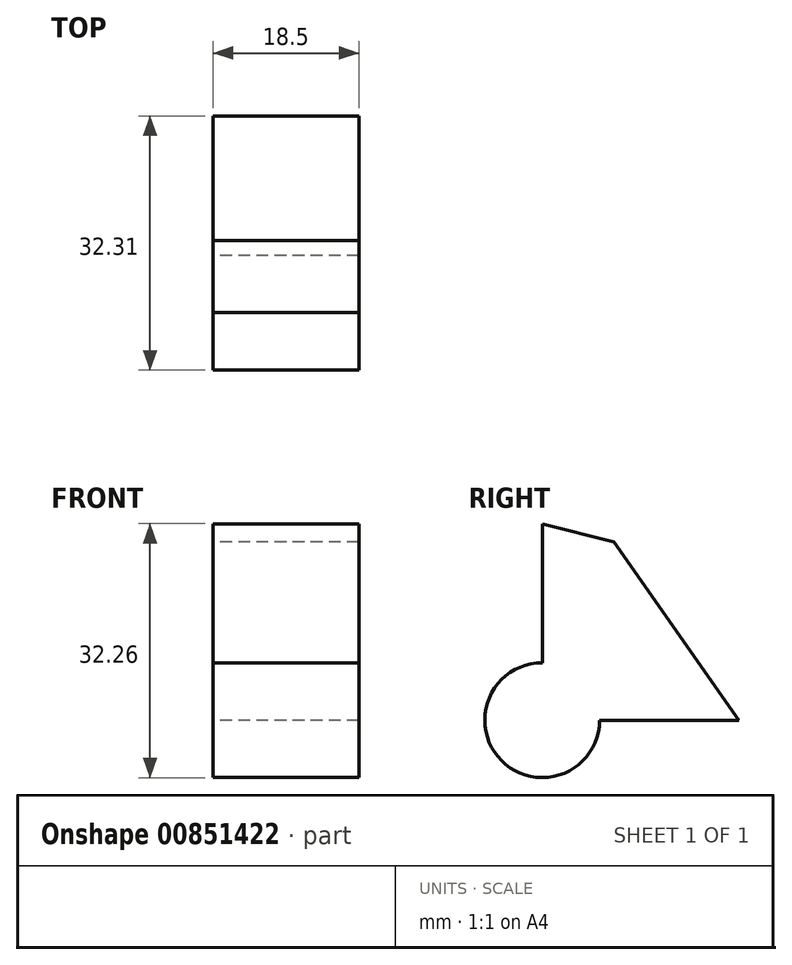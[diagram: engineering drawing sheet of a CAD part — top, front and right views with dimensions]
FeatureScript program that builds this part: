
annotation { "Feature Type Name" : "Feature", "Feature Type Description" : "" }
export const myFeature = defineFeature(function(context is Context, id is Id, definition is map)
    precondition{}
    {
        {
            var Q0;
            Q0=qCreatedBy(makeId("Right.planeOp"),FACE);
            var sketch = newSketch(context, id + "F0", { "sketchPlane" : qUnion([Q0])});
            skLineSegment(sketch, "E0", {"start": v(-48.68, 59.44) * mm, "end": v(-48.68, 34.44) * mm});
            skLineSegment(sketch, "E1", {"start": v(-48.68, 34.44) * mm, "end": v(-23.68, 34.44) * mm});
            skLineSegment(sketch, "E2", {"start": v(-23.68, 34.44) * mm, "end": v(-39.55, 57.1) * mm});
            skLineSegment(sketch, "E3", {"start": v(-39.55, 57.1) * mm, "end": v(-48.68, 59.44) * mm});
            skSolve(sketch);
        }
        {
            var Q0;
            Q0=makeQuery(id+"F0.imprint","IMPRINT",FACE,{"disambiguationData":[TD([[makeQuery(id+"F0.imprint","IMPRINT",EDGE,{"derivedFrom":sQuery(id+"F0.wireOp",EDGE,"E0")}),1.0]])]});
            extrude(context, id + "F1", {"entities" : qUnion([Q0]), "depth" : 18.5 * mm, "offsetDistance" : 25 * mm});
        }
        {
            var Q0;
            Q0=qCreatedBy(makeId("Right.planeOp"),FACE);
            var sketch = newSketch(context, id + "F2", { "sketchPlane" : qUnion([Q0])});
            skCircle(sketch, "E4", {"center": v(-48.7, 34.48) * mm, "radius": 7.3 * mm});
            skSolve(sketch);
        }
        {
            var Q0;
            Q0=makeQuery(id+"F2.imprint","IMPRINT",FACE,{"disambiguationData":[TD([[makeQuery(id+"F2.imprint","IMPRINT",EDGE,{"derivedFrom":sQuery(id+"F2.wireOp",EDGE,"E4")}),1.0]])]});
            extrude(context, id + "F3", {"entities" : qUnion([Q0]), "operationType" : NewBodyOperationType.ADD, "depth" : 18.5 * mm, "offsetDistance" : 25 * mm});
        }
    });
